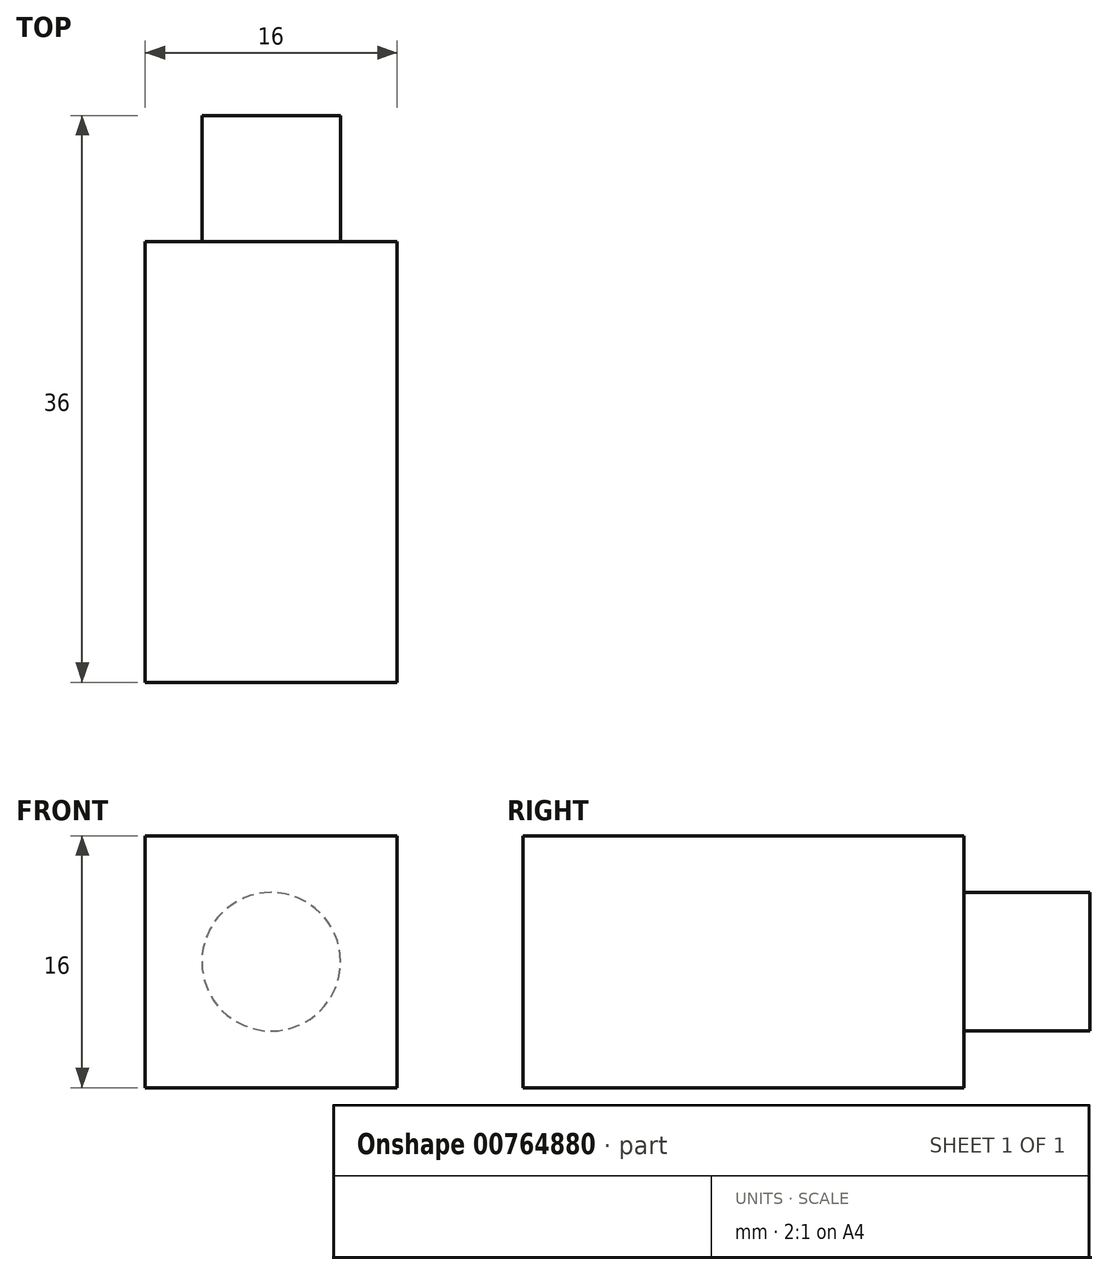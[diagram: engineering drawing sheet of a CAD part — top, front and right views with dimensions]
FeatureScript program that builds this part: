
annotation { "Feature Type Name" : "Feature", "Feature Type Description" : "" }
export const myFeature = defineFeature(function(context is Context, id is Id, definition is map)
    precondition{}
    {
        {
            var Q0;
            Q0=qCreatedBy(makeId("Front.planeOp"),FACE);
            var sketch = newSketch(context, id + "F0", { "sketchPlane" : qUnion([Q0])});
            skLineSegment(sketch, "E0.bottom", {"start": v(0, 0) * mm, "end": v(16, 0) * mm});
            skLineSegment(sketch, "E0.top", {"start": v(0, 16) * mm, "end": v(16, 16) * mm});
            skLineSegment(sketch, "E0.left", {"start": v(0, 0) * mm, "end": v(0, 16) * mm});
            skLineSegment(sketch, "E0.right", {"start": v(16, 0) * mm, "end": v(16, 16) * mm});
            skSolve(sketch);
        }
        {
            var Q0;
            Q0=makeQuery(id+"F0.imprint","IMPRINT",FACE,{"disambiguationData":[TD([[makeQuery(id+"F0.imprint","IMPRINT",EDGE,{"derivedFrom":sQuery(id+"F0.wireOp",EDGE,"E0.bottom")}),1.0]])]});
            extrude(context, id + "F1", {"entities" : qUnion([Q0]), "depth" : 28 * mm, "offsetDistance" : 25 * mm});
        }
        {
            var Q0;
            Q0=makeQuery(id+"F1.opExtrude","CAP_FACE",FACE,{"disambiguationData":[OSD([sQuery(id+"F0.wireOp",EDGE,"E0.bottom"),sQuery(id+"F0.wireOp",EDGE,"E0.top"),sQuery(id+"F0.wireOp",EDGE,"E0.left"),sQuery(id+"F0.wireOp",EDGE,"E0.right")])],"isStart":true});
            var sketch = newSketch(context, id + "F2", { "sketchPlane" : qUnion([Q0])});
            skLineSegment(sketch, "E1", {"start": v(-8, 16) * mm, "end": v(-8, 0) * mm, "construction": true});
            skLineSegment(sketch, "E2", {"start": v(0, 8) * mm, "end": v(-8, 8) * mm, "construction": true});
            skCircle(sketch, "E3", {"center": v(-8, 8) * mm, "radius": 4.4 * mm});
            skSolve(sketch);
        }
        {
            var Q0;
            Q0=makeQuery(id+"F2.imprint","IMPRINT",FACE,{"disambiguationData":[TD([[makeQuery(id+"F2.imprint","IMPRINT",EDGE,{"derivedFrom":sQuery(id+"F2.wireOp",EDGE,"E3")}),1.0]])]});
            extrude(context, id + "F3", {"entities" : qUnion([Q0]), "operationType" : NewBodyOperationType.ADD, "depth" : 8 * mm, "offsetDistance" : 25 * mm});
        }
    });
